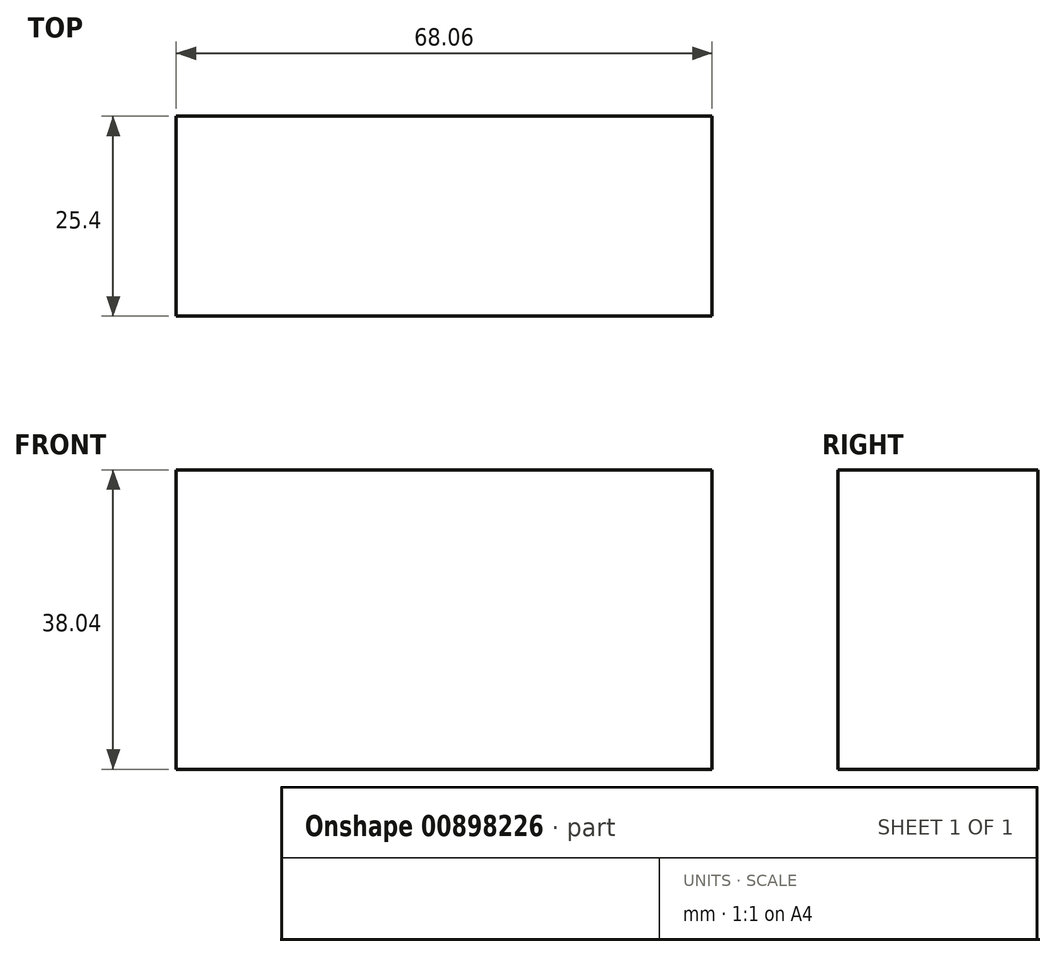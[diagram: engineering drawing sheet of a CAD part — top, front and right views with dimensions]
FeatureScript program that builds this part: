
annotation { "Feature Type Name" : "Feature", "Feature Type Description" : "" }
export const myFeature = defineFeature(function(context is Context, id is Id, definition is map)
    precondition{}
    {
        {
            var Q0;
            Q0=qCreatedBy(makeId("Front.planeOp"),FACE);
            var sketch = newSketch(context, id + "F0", { "sketchPlane" : qUnion([Q0])});
            skLineSegment(sketch, "E0.bottom", {"start": v(0, 0) * mm, "end": v(68.06, 0) * mm});
            skLineSegment(sketch, "E0.top", {"start": v(0, 38.04) * mm, "end": v(68.06, 38.04) * mm});
            skLineSegment(sketch, "E0.left", {"start": v(0, 0) * mm, "end": v(0, 38.04) * mm});
            skLineSegment(sketch, "E0.right", {"start": v(68.06, 0) * mm, "end": v(68.06, 38.04) * mm});
            skSolve(sketch);
        }
        {
            var Q0;
            Q0 = qSketchRegion(id + "F0", true);
            extrude(context, id + "F1", {"entities" : qUnion([Q0]), "depth" : 25.4 * mm, "offsetDistance" : 25.4 * mm});
        }
    });
